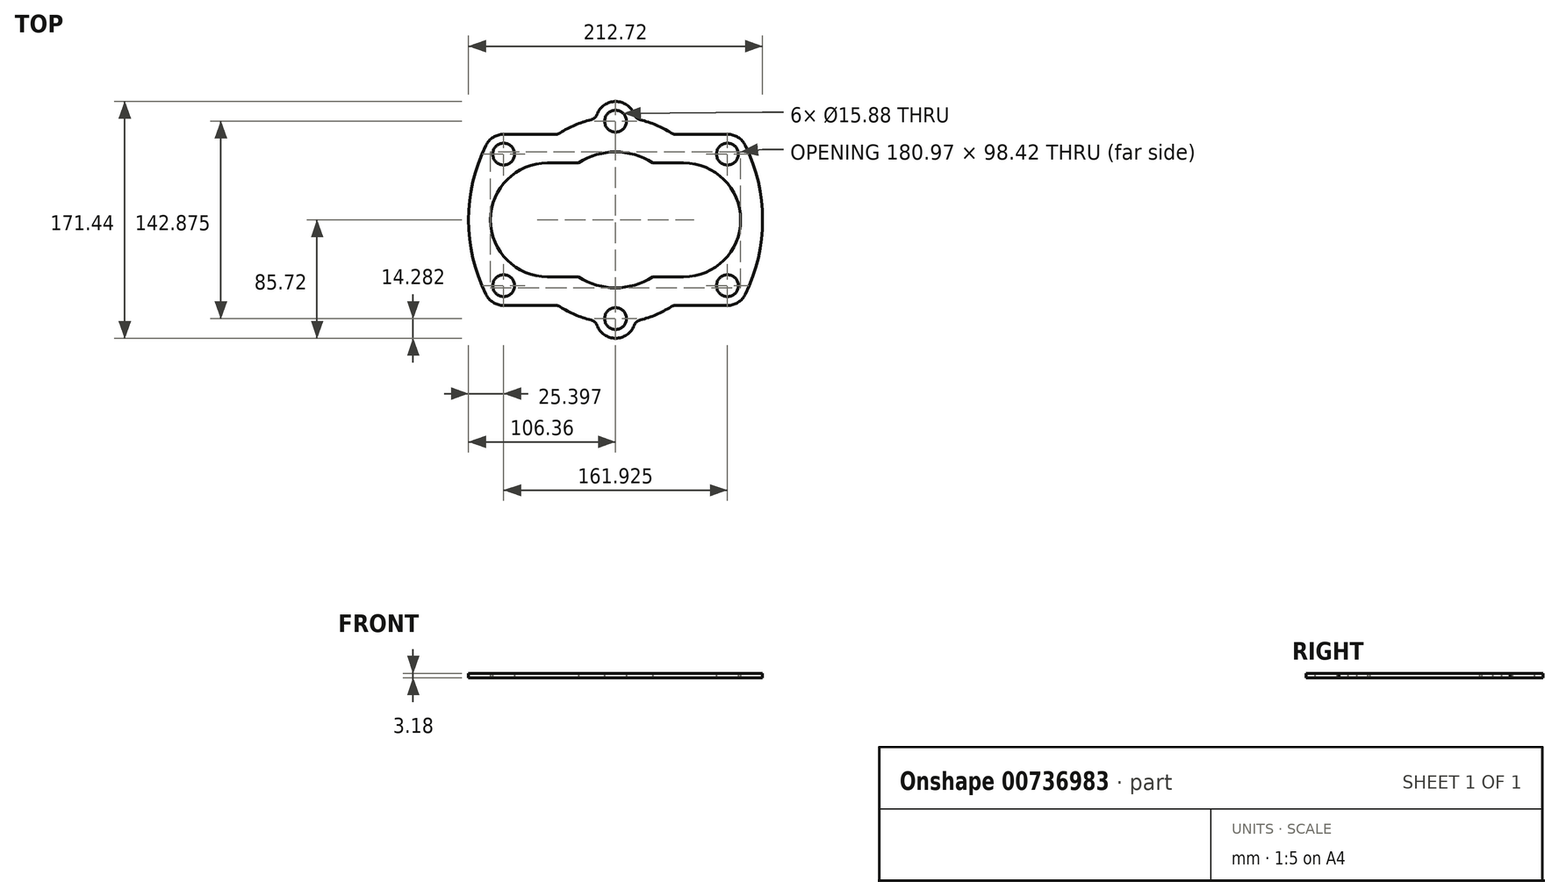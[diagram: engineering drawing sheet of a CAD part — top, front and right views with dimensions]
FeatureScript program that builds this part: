
annotation { "Feature Type Name" : "Feature", "Feature Type Description" : "" }
export const myFeature = defineFeature(function(context is Context, id is Id, definition is map)
    precondition{}
    {
        {
            var Q0;
            Q0=qCreatedBy(makeId("Top.planeOp"),FACE);
            var sketch = newSketch(context, id + "F0", { "sketchPlane" : qUnion([Q0])});
            skArc(sketch, "E0", {"start": v(-26.8, -41.27) * mm, "mid": v(0, -49.21) * mm, "end": v(26.8, -41.28) * mm});
            skArc(sketch, "E1", {"start": v(-49.21, 41.28) * mm, "mid": v(-90.49, 0) * mm, "end": v(-49.21, -41.28) * mm});
            skCircle(sketch, "E2", {"center": v(-80.96, 47.63) * mm, "radius": 7.94 * mm});
            skLineSegment(sketch, "E3", {"start": v(-49.21, 41.27) * mm, "end": v(-26.8, 41.27) * mm});
            skLineSegment(sketch, "E4.MirrorCS", {"start": v(-49.21, -41.28) * mm, "end": v(-26.8, -41.28) * mm});
            skLineSegment(sketch, "E5.MirrorCS", {"start": v(49.21, 41.28) * mm, "end": v(26.8, 41.28) * mm});
            skArc(sketch, "E6.MirrorC", {"start": v(49.21, 41.28) * mm, "mid": v(90.49, 0) * mm, "end": v(49.21, -41.28) * mm});
            skLineSegment(sketch, "E7.MirrorCS", {"start": v(49.21, -41.28) * mm, "end": v(26.8, -41.28) * mm});
            skLineSegment(sketch, "E8", {"start": v(-90.49, 0) * mm, "end": v(90.49, 0) * mm, "construction": true});
            skArc(sketch, "E9.trimOffspring", {"start": v(26.8, 41.27) * mm, "mid": v(0, 49.21) * mm, "end": v(-26.8, 41.28) * mm});
            skArc(sketch, "E10.0", {"start": v(-80.96, 61.91) * mm, "mid": v(-88.5, 59.76) * mm, "end": v(-93.77, 53.95) * mm});
            skArc(sketch, "E11.MirrorC", {"start": v(80.96, 61.91) * mm, "mid": v(88.5, 59.76) * mm, "end": v(93.77, 53.95) * mm});
            skCircle(sketch, "E12.MirrorC", {"center": v(80.96, 47.63) * mm, "radius": 7.94 * mm});
            skCircle(sketch, "E13", {"center": v(0, 71.44) * mm, "radius": 7.94 * mm});
            skPoint(sketch, "E13.centerSnap0", {"position": v(0, 49.21) * mm});
            skArc(sketch, "E14", {"start": v(13.4, 76.4) * mm, "mid": v(0, 85.72) * mm, "end": v(-13.4, 76.4) * mm});
            skArc(sketch, "E15.MirrorC", {"start": v(-80.96, -61.91) * mm, "mid": v(-88.5, -59.76) * mm, "end": v(-93.77, -53.95) * mm});
            skCircle(sketch, "E16.MirrorC", {"center": v(-80.96, -47.63) * mm, "radius": 7.94 * mm});
            skArc(sketch, "E17.MirrorC", {"start": v(13.4, -76.4) * mm, "mid": v(0, -85.72) * mm, "end": v(-13.4, -76.4) * mm});
            skCircle(sketch, "E18.MirrorC", {"center": v(0, -71.44) * mm, "radius": 7.94 * mm});
            skCircle(sketch, "E19.MirrorC", {"center": v(80.96, -47.63) * mm, "radius": 7.94 * mm});
            skArc(sketch, "E20.MirrorC", {"start": v(80.96, -61.91) * mm, "mid": v(88.5, -59.76) * mm, "end": v(93.77, -53.95) * mm});
            skArc(sketch, "E21", {"start": v(40.12, 62.9) * mm, "mid": v(29.37, 68.6) * mm, "end": v(17.83, 72.45) * mm});
            skLineSegment(sketch, "E22", {"start": v(-80.96, 61.91) * mm, "end": v(-43.53, 61.91) * mm});
            skLineSegment(sketch, "E23.MirrorCS", {"start": v(-80.96, -61.91) * mm, "end": v(-43.53, -61.91) * mm});
            skArc(sketch, "E24", {"start": v(93.77, -53.95) * mm, "mid": v(106.36, 0) * mm, "end": v(93.77, 53.95) * mm});
            skArc(sketch, "E25.MirrorCS", {"start": v(-93.77, -53.95) * mm, "mid": v(-106.36, 0) * mm, "end": v(-93.77, 53.95) * mm});
            skArc(sketch, "E26.trimOffspring", {"start": v(-40.12, -62.9) * mm, "mid": v(-29.37, -68.6) * mm, "end": v(-17.83, -72.45) * mm});
            skLineSegment(sketch, "E27.trimOffspring", {"start": v(43.53, -61.91) * mm, "end": v(80.96, -61.91) * mm});
            skLineSegment(sketch, "E28.trimOffspring", {"start": v(43.53, 61.91) * mm, "end": v(80.96, 61.91) * mm});
            skArc(sketch, "E29.trimOffspring", {"start": v(-17.83, 72.45) * mm, "mid": v(-29.37, 68.6) * mm, "end": v(-40.12, 62.9) * mm});
            skArc(sketch, "E30.trimOffspring", {"start": v(17.83, -72.45) * mm, "mid": v(29.37, -68.6) * mm, "end": v(40.12, -62.9) * mm});
            skPoint(sketch, "E31.visualSharp", {"position": v(-41.64, 61.91) * mm});
            skArc(sketch, "E31.filletArc", {"start": v(-43.53, 61.91) * mm, "mid": v(-41.76, 62.17) * mm, "end": v(-40.12, 62.9) * mm});
            skPoint(sketch, "E32.visualSharp", {"position": v(41.64, 61.91) * mm});
            skArc(sketch, "E32.filletArc", {"start": v(40.12, 62.9) * mm, "mid": v(41.76, 62.17) * mm, "end": v(43.53, 61.91) * mm});
            skPoint(sketch, "E33.visualSharp", {"position": v(-14.17, 73.25) * mm});
            skArc(sketch, "E33.filletArc", {"start": v(-17.83, 72.45) * mm, "mid": v(-15.12, 73.88) * mm, "end": v(-13.4, 76.4) * mm});
            skPoint(sketch, "E34.visualSharp", {"position": v(14.17, 73.25) * mm});
            skArc(sketch, "E34.filletArc", {"start": v(13.4, 76.4) * mm, "mid": v(15.12, 73.88) * mm, "end": v(17.83, 72.45) * mm});
            skPoint(sketch, "E35.visualSharp", {"position": v(-41.64, -61.91) * mm});
            skArc(sketch, "E35.filletArc", {"start": v(-40.12, -62.9) * mm, "mid": v(-41.76, -62.17) * mm, "end": v(-43.53, -61.91) * mm});
            skPoint(sketch, "E36.visualSharp", {"position": v(-14.17, -73.25) * mm});
            skArc(sketch, "E36.filletArc", {"start": v(-13.4, -76.4) * mm, "mid": v(-15.12, -73.88) * mm, "end": v(-17.83, -72.45) * mm});
            skPoint(sketch, "E37.visualSharp", {"position": v(14.17, -73.25) * mm});
            skArc(sketch, "E37.filletArc", {"start": v(17.83, -72.45) * mm, "mid": v(15.12, -73.88) * mm, "end": v(13.4, -76.4) * mm});
            skPoint(sketch, "E38.visualSharp", {"position": v(41.64, -61.91) * mm});
            skArc(sketch, "E38.filletArc", {"start": v(43.53, -61.91) * mm, "mid": v(41.76, -62.17) * mm, "end": v(40.12, -62.9) * mm});
            skLineSegment(sketch, "E39.bottom", {"start": v(-90.49, 57.15) * mm, "end": v(-71.44, 57.15) * mm, "construction": true});
            skLineSegment(sketch, "E39.top", {"start": v(-90.49, 38.1) * mm, "end": v(-71.44, 38.1) * mm, "construction": true});
            skLineSegment(sketch, "E39.left", {"start": v(-90.49, 57.15) * mm, "end": v(-90.49, 38.1) * mm, "construction": true});
            skLineSegment(sketch, "E39.right", {"start": v(-71.44, 57.15) * mm, "end": v(-71.44, 38.1) * mm, "construction": true});
            skLineSegment(sketch, "E40", {"start": v(-90.49, 57.15) * mm, "end": v(-71.44, 38.1) * mm, "construction": true});
            skLineSegment(sketch, "E41", {"start": v(-71.44, 57.15) * mm, "end": v(-90.49, 38.1) * mm, "construction": true});
            skLineSegment(sketch, "E42.bottom", {"start": v(71.44, 57.15) * mm, "end": v(90.49, 57.15) * mm, "construction": true});
            skLineSegment(sketch, "E42.top", {"start": v(71.44, 38.1) * mm, "end": v(90.49, 38.1) * mm, "construction": true});
            skLineSegment(sketch, "E42.left", {"start": v(71.44, 57.15) * mm, "end": v(71.44, 38.1) * mm, "construction": true});
            skLineSegment(sketch, "E42.right", {"start": v(90.49, 57.15) * mm, "end": v(90.49, 38.1) * mm, "construction": true});
            skLineSegment(sketch, "E43", {"start": v(71.44, 57.15) * mm, "end": v(90.49, 38.1) * mm, "construction": true});
            skLineSegment(sketch, "E44", {"start": v(90.49, 57.15) * mm, "end": v(71.44, 38.1) * mm, "construction": true});
            skSolve(sketch);
        }
        {
            var Q0;
            Q0=makeQuery(id+"F0.imprint","IMPRINT",FACE,{"disambiguationData":[TD([[makeQuery(id+"F0.imprint","IMPRINT",EDGE,{"derivedFrom":sQuery(id+"F0.wireOp",EDGE,"E0")}),-1.0]])]});
            extrude(context, id + "F1", {"entities" : qUnion([Q0]), "depth" : 3.17 * mm, "offsetDistance" : 25.4 * mm});
        }
    });
